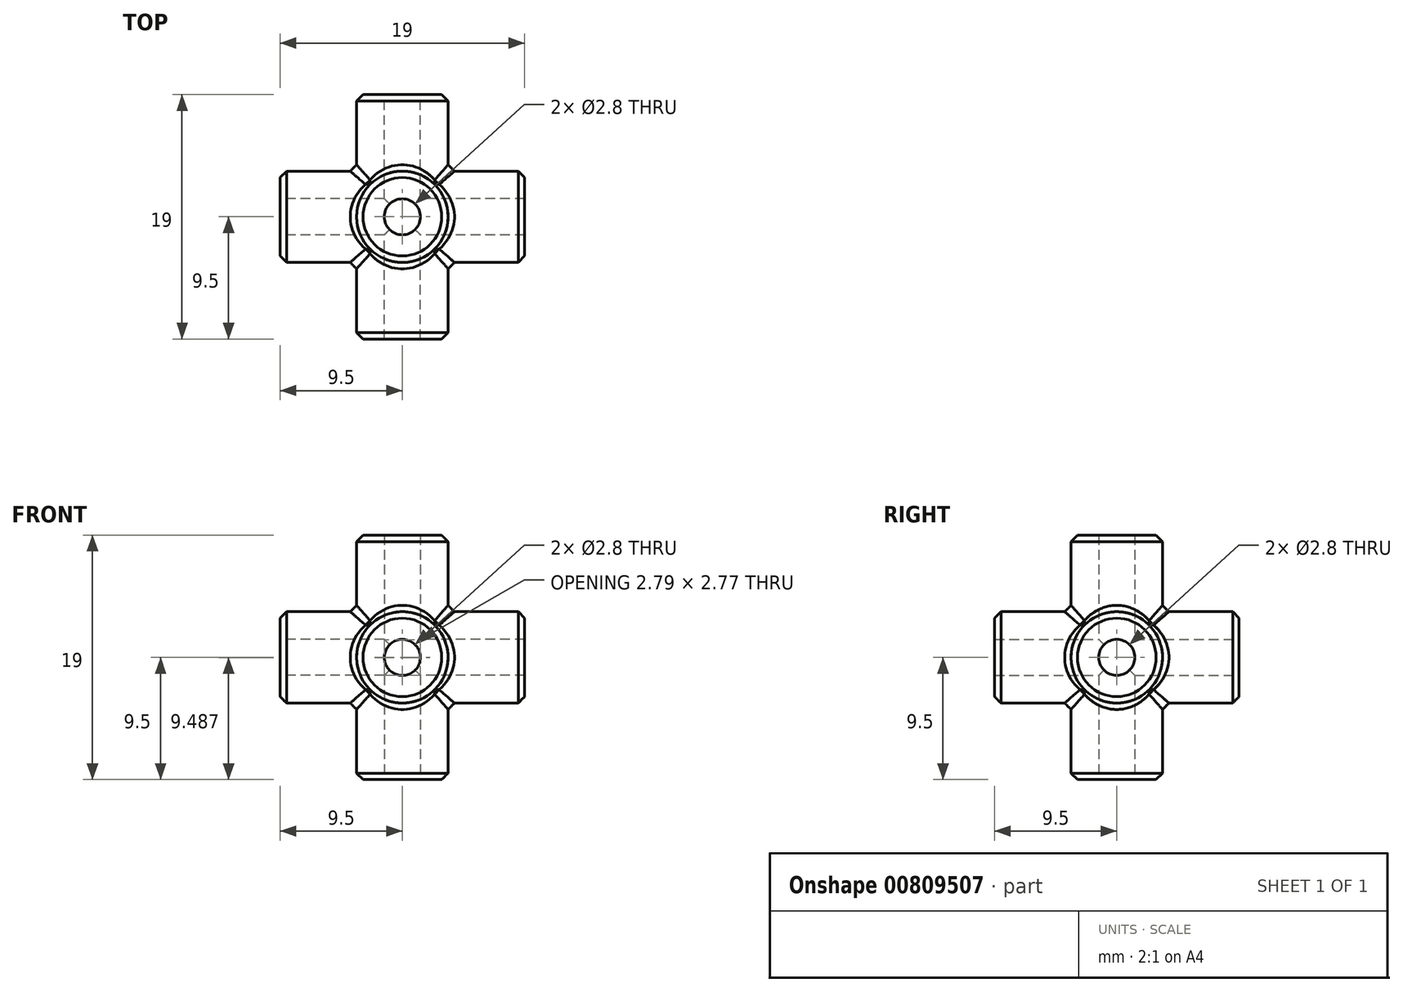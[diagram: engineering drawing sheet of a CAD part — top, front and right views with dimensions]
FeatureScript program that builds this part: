
annotation { "Feature Type Name" : "Feature", "Feature Type Description" : "" }
export const myFeature = defineFeature(function(context is Context, id is Id, definition is map)
    precondition{}
    {
        {
            var Q0;
            Q0=qCreatedBy(makeId("Front.planeOp"),FACE);
            var sketch = newSketch(context, id + "F0", { "sketchPlane" : qUnion([Q0])});
            skCircle(sketch, "E0", {"center": v(0, 0) * mm, "radius": 3.55 * mm});
            skSolve(sketch);
        }
        {
            var Q0;
            Q0=makeQuery(id+"F0.imprint","IMPRINT",FACE,{"disambiguationData":[TD([[makeQuery(id+"F0.imprint","IMPRINT",EDGE,{"derivedFrom":sQuery(id+"F0.wireOp",EDGE,"E0")}),1.0]])]});
            extrude(context, id + "F1", {"entities" : qUnion([Q0]), "endBound" : BoundingType.SYMMETRIC, "depth" : 19 * mm, "offsetDistance" : 25.4 * mm});
        }
        {
            var Q0;
            Q0=qCreatedBy(makeId("Front.planeOp"),FACE);
            var sketch = newSketch(context, id + "F2", { "sketchPlane" : qUnion([Q0])});
            skCircle(sketch, "E1", {"center": v(0, 0) * mm, "radius": 1.4 * mm});
            skSolve(sketch);
        }
        {
            var Q0;
            Q0 = qSketchRegion(id + "F2", true);
            extrude(context, id + "F3", {"entities" : qUnion([Q0]), "endBound" : BoundingType.SYMMETRIC, "depth" : 20 * mm, "offsetDistance" : 25 * mm});
        }
        {
            var Q0;
            Q0=qCreatedBy(makeId("Front.planeOp"),FACE);
            var sketch = newSketch(context, id + "F4", { "sketchPlane" : qUnion([Q0])});
            skLineSegment(sketch, "E2.bottom", {"start": v(0, 0) * mm, "end": v(10, 0) * mm});
            skLineSegment(sketch, "E2.top", {"start": v(0, 10) * mm, "end": v(10, 10) * mm});
            skLineSegment(sketch, "E2.left", {"start": v(0, 0) * mm, "end": v(0, 10) * mm});
            skLineSegment(sketch, "E2.right", {"start": v(10, 0) * mm, "end": v(10, 10) * mm});
            skSolve(sketch);
        }
        {
            var Q0;
            Q0 = qSketchRegion(id + "F4", true);
            extrude(context, id + "F5", {"entities" : qUnion([Q0]), "depth" : 10 * mm, "offsetDistance" : 25 * mm});
        }
        {
            var Q0;
            Q0=qCreatedBy(makeId("Origin.pointOp"),VERTEX);
            var Q1;
            Q1=makeQuery(id+"F5.opExtrude","CAP_VERTEX",VERTEX,{"disambiguationData":[OSD([sQuery(id+"F4.wireOp",EDGE,"E2.top"),sQuery(id+"F4.wireOp",EDGE,"E2.right")])],"isStart":false});
            var Q2;
            Q2=makeQuery(id+"F5.opExtrude","CAP_VERTEX",VERTEX,{"disambiguationData":[OSD([sQuery(id+"F4.wireOp",EDGE,"E2.bottom"),sQuery(id+"F4.wireOp",EDGE,"E2.right")])],"isStart":false});
            cPlane(context, id + "F6", {"entities" : qUnion([Q0, Q1, Q2]), "cplaneType" : CPlaneType.THREE_POINT, "offset" : 25 * mm, "width" : 150 * mm, "height" : 150 * mm});
        }
        {
            var Q0;
            Q0=qCreatedBy(id+"F6.planeOp",FACE);
            var sketch = newSketch(context, id + "F7", { "sketchPlane" : qUnion([Q0])});
            skLineSegment(sketch, "E3", {"start": v(0, 0) * mm, "end": v(14.14, 10) * mm});
            skSolve(sketch);
        }
        {
            var Q0;
            Q0=makeQuery(id+"F5.opExtrude","SWEPT_BODY",BODY,{"disambiguationData":[OSD([sQuery(id+"F4.wireOp",EDGE,"E2.bottom"),sQuery(id+"F4.wireOp",EDGE,"E2.top"),sQuery(id+"F4.wireOp",EDGE,"E2.left"),sQuery(id+"F4.wireOp",EDGE,"E2.right")])]});
            deleteBodies(context, id + "F8", {"entities" : qUnion([Q0])});
        }
        {
            var Q0;
            Q0=makeQuery(id+"F3.opExtrude","SWEPT_BODY",BODY,{"disambiguationData":[OSD([sQuery(id+"F2.wireOp",EDGE,"E1")])]});
            var Q1;
            Q1=makeQuery(id+"F1.opExtrude","SWEPT_BODY",BODY,{"disambiguationData":[OSD([sQuery(id+"F0.wireOp",EDGE,"E0")])]});
            var Q2;
            Q2=sQuery(id+"F7.wireOp",EDGE,"E3");
            circularPattern(context, id + "F9", {"entities" : qUnion([Q0, Q1]), "axis" : qUnion([Q2]), "angle" : 360 * degree, "instanceCount" : 3, "equalSpace" : true});
        }
        {
            var Q0;
            Q0=makeQuery(id+"F1.opExtrude","SWEPT_BODY",BODY,{"disambiguationData":[OSD([sQuery(id+"F0.wireOp",EDGE,"E0")])]});
            var Q1;
            Q1=makeQuery(id+"F9.opPattern","COPY",BODY,{"derivedFrom":makeQuery(id+"F1.opExtrude","SWEPT_BODY",BODY,{"disambiguationData":[OSD([sQuery(id+"F0.wireOp",EDGE,"E0")])]}),"instanceName":"1"});
            var Q2;
            Q2=makeQuery(id+"F9.opPattern","COPY",BODY,{"derivedFrom":makeQuery(id+"F1.opExtrude","SWEPT_BODY",BODY,{"disambiguationData":[OSD([sQuery(id+"F0.wireOp",EDGE,"E0")])]}),"instanceName":"2"});
            booleanBodies(context, id + "F10", {"operationType" : BooleanOperationType.UNION, "tools" : qUnion([Q0, Q1, Q2])});
        }
        {
            var Q0;
            Q0=makeQuery(id+"F3.opExtrude","SWEPT_BODY",BODY,{"disambiguationData":[OSD([sQuery(id+"F2.wireOp",EDGE,"E1")])]});
            var Q1;
            Q1=makeQuery(id+"F9.opPattern","COPY",BODY,{"derivedFrom":makeQuery(id+"F3.opExtrude","SWEPT_BODY",BODY,{"disambiguationData":[OSD([sQuery(id+"F2.wireOp",EDGE,"E1")])]}),"instanceName":"1"});
            var Q2;
            Q2=makeQuery(id+"F9.opPattern","COPY",BODY,{"derivedFrom":makeQuery(id+"F3.opExtrude","SWEPT_BODY",BODY,{"disambiguationData":[OSD([sQuery(id+"F2.wireOp",EDGE,"E1")])]}),"instanceName":"2"});
            var Q3;
            Q3=makeQuery(id+"F1.opExtrude","SWEPT_BODY",BODY,{"disambiguationData":[OSD([sQuery(id+"F0.wireOp",EDGE,"E0")])]});
            booleanBodies(context, id + "F11", {"operationType" : BooleanOperationType.SUBTRACTION, "tools" : qUnion([Q0, Q1, Q2]), "targets" : qUnion([Q3])});
        }
        {
            var Q0;
            {var subQ0=sQuery(id+"F0.wireOp",EDGE,"E0");var subQ1=makeQuery(id+"F1.opExtrude","SWEPT_FACE",FACE,{"disambiguationData":[OSD([subQ0])]});Q0=makeQuery(id+"F10.opBoolean","SPLIT",FACE,{"disambiguationData":[TD([makeQuery(id+"F9.opPattern","COPY",FACE,{"derivedFrom":makeQuery(id+"F1.opExtrude","CAP_FACE",FACE,{"disambiguationData":[OSD([subQ0])],"isStart":false}),"instanceName":"2"})])],"derivedFrom":makeQuery(id+"F9.opPattern","COPY",FACE,{"derivedFrom":subQ1,"instanceName":"2"})});}
            var Q1;
            {var subQ0=sQuery(id+"F0.wireOp",EDGE,"E0");var subQ1=makeQuery(id+"F1.opExtrude","SWEPT_FACE",FACE,{"disambiguationData":[OSD([subQ0])]});Q1=makeQuery(id+"F10.opBoolean","SPLIT",FACE,{"disambiguationData":[TD([makeQuery(id+"F9.opPattern","COPY",FACE,{"derivedFrom":makeQuery(id+"F1.opExtrude","CAP_FACE",FACE,{"disambiguationData":[OSD([subQ0])],"isStart":true}),"instanceName":"2"})])],"derivedFrom":makeQuery(id+"F9.opPattern","COPY",FACE,{"derivedFrom":subQ1,"instanceName":"2"})});}
            var Q2;
            {var subQ0=sQuery(id+"F0.wireOp",EDGE,"E0");var subQ1=makeQuery(id+"F1.opExtrude","SWEPT_FACE",FACE,{"disambiguationData":[OSD([subQ0])]});Q2=makeQuery(id+"F10.opBoolean","SPLIT",FACE,{"disambiguationData":[TD([makeQuery(id+"F9.opPattern","COPY",FACE,{"derivedFrom":makeQuery(id+"F1.opExtrude","CAP_FACE",FACE,{"disambiguationData":[OSD([subQ0])],"isStart":false}),"instanceName":"1"})])],"derivedFrom":makeQuery(id+"F9.opPattern","COPY",FACE,{"derivedFrom":subQ1,"instanceName":"1"})});}
            var Q3;
            {var subQ0=sQuery(id+"F0.wireOp",EDGE,"E0");var subQ1=makeQuery(id+"F1.opExtrude","SWEPT_FACE",FACE,{"disambiguationData":[OSD([subQ0])]});Q3=makeQuery(id+"F10.opBoolean","SPLIT",FACE,{"disambiguationData":[TD([makeQuery(id+"F1.opExtrude","CAP_FACE",FACE,{"disambiguationData":[OSD([subQ0])],"isStart":false})])],"derivedFrom":subQ1});}
            var Q4;
            {var subQ0=sQuery(id+"F0.wireOp",EDGE,"E0");var subQ1=makeQuery(id+"F1.opExtrude","SWEPT_FACE",FACE,{"disambiguationData":[OSD([subQ0])]});Q4=makeQuery(id+"F10.opBoolean","SPLIT",FACE,{"disambiguationData":[TD([makeQuery(id+"F9.opPattern","COPY",FACE,{"derivedFrom":makeQuery(id+"F1.opExtrude","CAP_FACE",FACE,{"disambiguationData":[OSD([subQ0])],"isStart":true}),"instanceName":"1"})])],"derivedFrom":makeQuery(id+"F9.opPattern","COPY",FACE,{"derivedFrom":subQ1,"instanceName":"1"})});}
            var Q5;
            {var subQ0=sQuery(id+"F0.wireOp",EDGE,"E0");var subQ1=makeQuery(id+"F1.opExtrude","SWEPT_FACE",FACE,{"disambiguationData":[OSD([subQ0])]});Q5=makeQuery(id+"F10.opBoolean","SPLIT",FACE,{"disambiguationData":[TD([makeQuery(id+"F1.opExtrude","CAP_FACE",FACE,{"disambiguationData":[OSD([subQ0])],"isStart":true})])],"derivedFrom":subQ1});}
            chamfer(context, id + "F12", {"entities" : qUnion([Q0, Q1, Q2, Q3, Q4, Q5]), "width" : 0.5 * mm, "tangentPropagation" : true});
        }
    });
